# Revit family: Workstations-Multi_Level-Teknion-B_AUHB_L_Shape_Desk_for_U_Shape_High_Secondary_Desk_Bevel_Bases-R2018
name_source: partatom
category: Furniture
revit_build: Autodesk Revit 2018 (Build: 20190510_1515(x64)
units: mm (PartAtom-declared; Revit-internal decimal feet)

## family parameters
Always vertical = Yes
Cut with Voids When Loaded = No
OmniClass Number = 23.40.20.00
OmniClass Title = General Furniture and Specialties
Room Calculation Point = No
Shared = Yes
Work Plane-Based = No

## types (5) — shared parameters
Assembly Code = E2020200
Manufacturer = Teknion
Manufacturer Fax = 416.661.4586
Part Number = B_AUHB
Product Documentation Link = https://www.teknion.com
Product Documentation Link #2 = https://www.teknion.com
Product Documentation Link #3 = https://www.teknion.com
Product Documentation Link #4 = https://www.teknion.com
Product Line = Expansion Casegoods
Product Page URL = https://www.teknion.com
Rectangular Grommet On Return = Yes
Series = Expansion Casegoods
Sustainability Data = https://www.teknion.com
URL = www.teknion.com
Unit Weight URL = http://www.teknion.com
Warranty = http://www.teknion.com

## per-type parameters (varying)
| type | Description | Model | Rectangular Grommet on Desk | Square Grommet on Desk | Square Grommet on Desk Cut Hole Depth | Square Grommet on Return | Square Grommet on Return Cut Depth |
| Rectangular Grommet on Desk & Return | Height-Adjustable L-Shape Desk for U-Shape Workstation - High Secondary Desk - Bevel Bases, Extended Range - 29" to 48", Rectangular on Desk & Return | B_AUHBE____O_ | Yes | No | 0.5 " | No | 0.5 " |
| Rectangular Grommet on Return with Square Cutout on Return | Height-Adjustable L-Shape Desk for U-Shape Workstation - High Secondary Desk - Bevel Bases, Extended Range - 29" to 48", Rectangular & Square on Return | B_AUHBE____A_ | No | No | 0.5 " | Yes | 4 " |
| Rectangular Grommet on Return | Height-Adjustable L-Shape Desk for U-Shape Workstation - High Secondary Desk - Bevel Bases, Extended Range - 29" to 48", Rectangular Grommet on Return | B_AUHBE____N_ | No | No | 0.5 " | No | 0.5 " |
| Rectangular Grommet on Desk & Return with Square Cutout on Desk | Height-Adjustable L-Shape Desk for U-Shape Workstation - High Secondary Desk - Bevel Bases, Extended Range - 29" to 48", Rectangular on Desk & Return/Square on Desk | B_AUHBE____P_ | Yes | Yes | 4 " | No | 0.5 " |
| Rectangular Grommet on Desk & Return with Square Cutout on Return | Height-Adjustable L-Shape Desk for U-Shape Workstation - High Secondary Desk - Bevel Bases, Extended Range - 29" to 48", Rectangular on Desk & Return/Square on Return | B_AUHBE____Q_ | Yes | No | 0.5 " | Yes | 4 " |

## geometry (parser evidence)
native form markers: Sweep x3
no freeform markers — native parametric forms only
